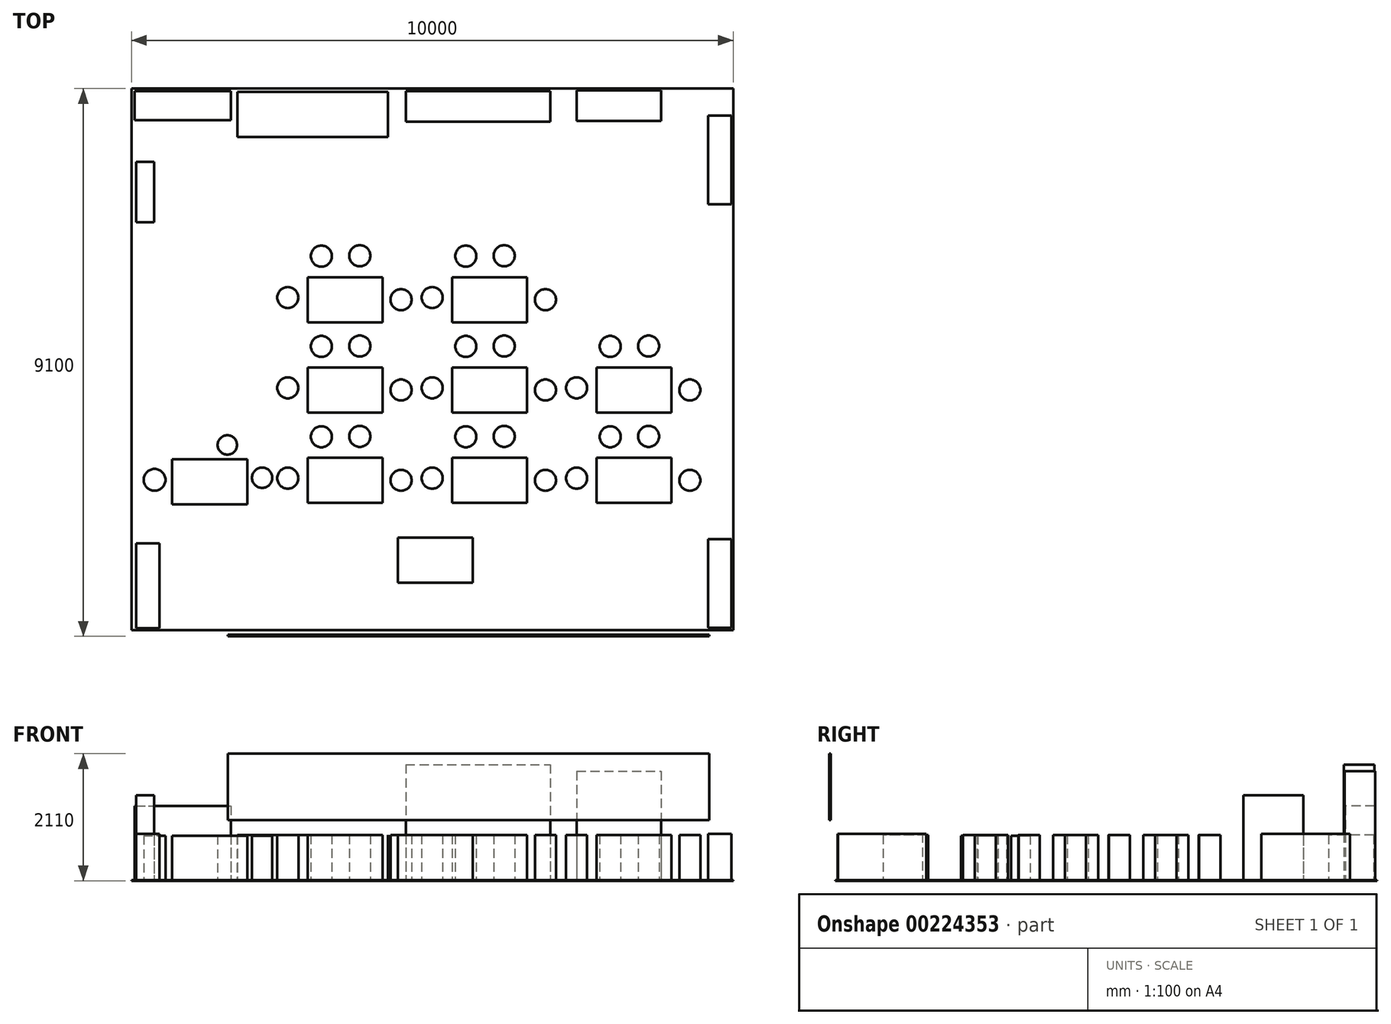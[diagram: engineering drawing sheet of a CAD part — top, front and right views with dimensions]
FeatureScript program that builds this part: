
annotation { "Feature Type Name" : "Feature", "Feature Type Description" : "" }
export const myFeature = defineFeature(function(context is Context, id is Id, definition is map)
    precondition{}
    {
        {
            var Q0;
            Q0=qCreatedBy(makeId("Top.planeOp"),FACE);
            var sketch = newSketch(context, id + "F0", { "sketchPlane" : qUnion([Q0])});
            skLineSegment(sketch, "E0.bottom", {"start": v(-5000, 4500) * mm, "end": v(5000, 4500) * mm});
            skLineSegment(sketch, "E0.top", {"start": v(-5000, -4500) * mm, "end": v(5000, -4500) * mm});
            skLineSegment(sketch, "E0.left", {"start": v(-5000, 4500) * mm, "end": v(-5000, -4500) * mm});
            skLineSegment(sketch, "E0.right", {"start": v(5000, 4500) * mm, "end": v(5000, -4500) * mm});
            skSolve(sketch);
        }
        {
            var Q0;
            Q0=makeQuery(id+"F0.imprint","IMPRINT",FACE,{"disambiguationData":[TD([[makeQuery(id+"F0.imprint","IMPRINT",EDGE,{"derivedFrom":sQuery(id+"F0.wireOp",EDGE,"E0.bottom")}),-1.0]])]});
            extrude(context, id + "F1", {"entities" : qUnion([Q0]), "oppositeDirection" : true, "depth" : 10 * mm});
        }
        {
            var Q0;
            Q0=qCreatedBy(makeId("Top.planeOp"),FACE);
            var sketch = newSketch(context, id + "F2", { "sketchPlane" : qUnion([Q0])});
            skLineSegment(sketch, "E1.bottom", {"start": v(-575.24, -2960.77) * mm, "end": v(674.76, -2960.77) * mm});
            skLineSegment(sketch, "E1.top", {"start": v(-575.24, -3710.77) * mm, "end": v(674.76, -3710.77) * mm});
            skLineSegment(sketch, "E1.left", {"start": v(-575.24, -2960.77) * mm, "end": v(-575.24, -3710.77) * mm});
            skLineSegment(sketch, "E1.right", {"start": v(674.76, -2960.77) * mm, "end": v(674.76, -3710.77) * mm});
            skLineSegment(sketch, "E2.bottom", {"start": v(2726.92, -1633.07) * mm, "end": v(3976.92, -1633.07) * mm});
            skLineSegment(sketch, "E2.top", {"start": v(2726.92, -2383.07) * mm, "end": v(3976.92, -2383.07) * mm});
            skLineSegment(sketch, "E2.left", {"start": v(2726.92, -1633.07) * mm, "end": v(2726.92, -2383.07) * mm});
            skLineSegment(sketch, "E2.right", {"start": v(3976.92, -1633.07) * mm, "end": v(3976.92, -2383.07) * mm});
            skCircle(sketch, "E3", {"center": v(3594.57, -1278.37) * mm, "radius": 175 * mm});
            skCircle(sketch, "E4", {"center": v(2398.6, -1972.2) * mm, "radius": 175 * mm});
            skCircle(sketch, "E5", {"center": v(2957.34, -1284.58) * mm, "radius": 175 * mm});
            skCircle(sketch, "E6", {"center": v(4280.4, -2008.07) * mm, "radius": 175 * mm});
            skCircle(sketch, "E7.0.1.0", {"center": v(3594.57, 221.63) * mm, "radius": 175 * mm});
            skCircle(sketch, "E7.0.1.1", {"center": v(4280.4, -508.07) * mm, "radius": 175 * mm});
            skLineSegment(sketch, "E7.0.1.2", {"start": v(3976.92, -133.07) * mm, "end": v(3976.92, -883.07) * mm});
            skCircle(sketch, "E7.0.1.3", {"center": v(2957.34, 215.42) * mm, "radius": 175 * mm});
            skLineSegment(sketch, "E7.0.1.4", {"start": v(2726.92, -133.07) * mm, "end": v(2726.92, -883.07) * mm});
            skCircle(sketch, "E7.0.1.5", {"center": v(2398.6, -472.2) * mm, "radius": 175 * mm});
            skLineSegment(sketch, "E7.0.1.6", {"start": v(2726.92, -883.07) * mm, "end": v(3976.92, -883.07) * mm});
            skLineSegment(sketch, "E7.0.1.7", {"start": v(2726.92, -133.07) * mm, "end": v(3976.92, -133.07) * mm});
            skCircle(sketch, "E7.1.0.0", {"center": v(1194.57, -1278.37) * mm, "radius": 175 * mm});
            skCircle(sketch, "E7.1.0.1", {"center": v(1880.4, -2008.07) * mm, "radius": 175 * mm});
            skLineSegment(sketch, "E7.1.0.2", {"start": v(1576.92, -1633.07) * mm, "end": v(1576.92, -2383.07) * mm});
            skCircle(sketch, "E7.1.0.3", {"center": v(557.34, -1284.58) * mm, "radius": 175 * mm});
            skLineSegment(sketch, "E7.1.0.4", {"start": v(326.92, -1633.07) * mm, "end": v(326.92, -2383.07) * mm});
            skCircle(sketch, "E7.1.0.5", {"center": v(-1.4, -1972.2) * mm, "radius": 175 * mm});
            skLineSegment(sketch, "E7.1.0.6", {"start": v(326.92, -2383.07) * mm, "end": v(1576.92, -2383.07) * mm});
            skLineSegment(sketch, "E7.1.0.7", {"start": v(326.92, -1633.07) * mm, "end": v(1576.92, -1633.07) * mm});
            skCircle(sketch, "E7.1.1.0", {"center": v(1194.57, 221.63) * mm, "radius": 175 * mm});
            skCircle(sketch, "E7.1.1.1", {"center": v(1880.4, -508.07) * mm, "radius": 175 * mm});
            skLineSegment(sketch, "E7.1.1.2", {"start": v(1576.92, -133.07) * mm, "end": v(1576.92, -883.07) * mm});
            skCircle(sketch, "E7.1.1.3", {"center": v(557.34, 215.42) * mm, "radius": 175 * mm});
            skLineSegment(sketch, "E7.1.1.4", {"start": v(326.92, -133.07) * mm, "end": v(326.92, -883.07) * mm});
            skCircle(sketch, "E7.1.1.5", {"center": v(-1.4, -472.2) * mm, "radius": 175 * mm});
            skLineSegment(sketch, "E7.1.1.6", {"start": v(326.92, -883.07) * mm, "end": v(1576.92, -883.07) * mm});
            skLineSegment(sketch, "E7.1.1.7", {"start": v(326.92, -133.07) * mm, "end": v(1576.92, -133.07) * mm});
            skCircle(sketch, "E7.1.2.0", {"center": v(1194.57, 1721.63) * mm, "radius": 175 * mm});
            skCircle(sketch, "E7.1.2.1", {"center": v(1880.4, 991.93) * mm, "radius": 175 * mm});
            skLineSegment(sketch, "E7.1.2.2", {"start": v(1576.92, 1366.93) * mm, "end": v(1576.92, 616.93) * mm});
            skCircle(sketch, "E7.1.2.3", {"center": v(557.34, 1715.42) * mm, "radius": 175 * mm});
            skLineSegment(sketch, "E7.1.2.4", {"start": v(326.92, 1366.93) * mm, "end": v(326.92, 616.93) * mm});
            skCircle(sketch, "E7.1.2.5", {"center": v(-1.4, 1027.8) * mm, "radius": 175 * mm});
            skLineSegment(sketch, "E7.1.2.6", {"start": v(326.92, 616.93) * mm, "end": v(1576.92, 616.93) * mm});
            skLineSegment(sketch, "E7.1.2.7", {"start": v(326.92, 1366.93) * mm, "end": v(1576.92, 1366.93) * mm});
            skCircle(sketch, "E7.2.0.0", {"center": v(-1205.43, -1278.37) * mm, "radius": 175 * mm});
            skCircle(sketch, "E7.2.0.1", {"center": v(-519.6, -2008.07) * mm, "radius": 175 * mm});
            skLineSegment(sketch, "E7.2.0.2", {"start": v(-823.08, -1633.07) * mm, "end": v(-823.08, -2383.07) * mm});
            skCircle(sketch, "E7.2.0.3", {"center": v(-1842.66, -1284.58) * mm, "radius": 175 * mm});
            skLineSegment(sketch, "E7.2.0.4", {"start": v(-2073.08, -1633.07) * mm, "end": v(-2073.08, -2383.07) * mm});
            skCircle(sketch, "E7.2.0.5", {"center": v(-2401.4, -1972.2) * mm, "radius": 175 * mm});
            skLineSegment(sketch, "E7.2.0.6", {"start": v(-2073.08, -2383.07) * mm, "end": v(-823.08, -2383.07) * mm});
            skLineSegment(sketch, "E7.2.0.7", {"start": v(-2073.08, -1633.07) * mm, "end": v(-823.08, -1633.07) * mm});
            skCircle(sketch, "E7.2.1.0", {"center": v(-1205.43, 221.63) * mm, "radius": 175 * mm});
            skCircle(sketch, "E7.2.1.1", {"center": v(-519.6, -508.07) * mm, "radius": 175 * mm});
            skLineSegment(sketch, "E7.2.1.2", {"start": v(-823.08, -133.07) * mm, "end": v(-823.08, -883.07) * mm});
            skCircle(sketch, "E7.2.1.3", {"center": v(-1842.66, 215.42) * mm, "radius": 175 * mm});
            skLineSegment(sketch, "E7.2.1.4", {"start": v(-2073.08, -133.07) * mm, "end": v(-2073.08, -883.07) * mm});
            skCircle(sketch, "E7.2.1.5", {"center": v(-2401.4, -472.2) * mm, "radius": 175 * mm});
            skLineSegment(sketch, "E7.2.1.6", {"start": v(-2073.08, -883.07) * mm, "end": v(-823.08, -883.07) * mm});
            skLineSegment(sketch, "E7.2.1.7", {"start": v(-2073.08, -133.07) * mm, "end": v(-823.08, -133.07) * mm});
            skCircle(sketch, "E7.2.2.0", {"center": v(-1205.43, 1721.63) * mm, "radius": 175 * mm});
            skCircle(sketch, "E7.2.2.1", {"center": v(-519.6, 991.93) * mm, "radius": 175 * mm});
            skLineSegment(sketch, "E7.2.2.2", {"start": v(-823.08, 1366.93) * mm, "end": v(-823.08, 616.93) * mm});
            skCircle(sketch, "E7.2.2.3", {"center": v(-1842.66, 1715.42) * mm, "radius": 175 * mm});
            skLineSegment(sketch, "E7.2.2.4", {"start": v(-2073.08, 1366.93) * mm, "end": v(-2073.08, 616.93) * mm});
            skCircle(sketch, "E7.2.2.5", {"center": v(-2401.4, 1027.8) * mm, "radius": 175 * mm});
            skLineSegment(sketch, "E7.2.2.6", {"start": v(-2073.08, 616.93) * mm, "end": v(-823.08, 616.93) * mm});
            skLineSegment(sketch, "E7.2.2.7", {"start": v(-2073.08, 1366.93) * mm, "end": v(-823.08, 1366.93) * mm});
            skLineSegment(sketch, "E7.direction1", {"start": v(2726.92, -2383.07) * mm, "end": v(326.92, -2383.07) * mm, "construction": true});
            skLineSegment(sketch, "E7.direction2", {"start": v(2726.92, -2383.07) * mm, "end": v(2726.92, -883.07) * mm, "construction": true});
            skPoint(sketch, "E8", {"position": v(3976.92, -508.07) * mm});
            skSolve(sketch);
        }
        {
            var Q0;
            Q0=qSketchRegion(id+"F2",true);
            extrude(context, id + "F3", {"entities" : qUnion([Q0]), "operationType" : NewBodyOperationType.ADD, "depth" : 750 * mm});
        }
        {
            var Q0;
            Q0=qCreatedBy(makeId("Front.planeOp"),FACE);
            cPlane(context, id + "F4", {"entities" : qUnion([Q0]), "cplaneType" : CPlaneType.OFFSET, "offset" : 4500 * mm, "width" : 150 * mm, "height" : 150 * mm});
        }
        {
            var Q0;
            Q0=qCreatedBy(id+"F4.planeOp",FACE);
            var sketch = newSketch(context, id + "F5", { "sketchPlane" : qUnion([Q0])});
            skLineSegment(sketch, "E9.bottom", {"start": v(-3400, 2100) * mm, "end": v(4600, 2100) * mm});
            skLineSegment(sketch, "E9.top", {"start": v(-3400, 1000) * mm, "end": v(4600, 1000) * mm});
            skLineSegment(sketch, "E9.left", {"start": v(-3400, 2100) * mm, "end": v(-3400, 1000) * mm});
            skLineSegment(sketch, "E9.right", {"start": v(4600, 2100) * mm, "end": v(4600, 1000) * mm});
            skSolve(sketch);
        }
        {
            var Q0;
            Q0=qSketchRegion(id+"F5",true);
            extrude(context, id + "F6", {"entities" : qUnion([Q0]), "oppositeDirection" : true, "depth" : 25 * mm});
        }
        {
            var Q0;
            Q0=qCreatedBy(makeId("Top.planeOp"),FACE);
            var sketch = newSketch(context, id + "F7", { "sketchPlane" : qUnion([Q0])});
            skLineSegment(sketch, "E10.bottom", {"start": v(-4950, 4456.62) * mm, "end": v(-4150, 4456.62) * mm});
            skLineSegment(sketch, "E10.top", {"start": v(-4950, 3976.62) * mm, "end": v(-4150, 3976.62) * mm});
            skLineSegment(sketch, "E10.left", {"start": v(-4950, 4456.62) * mm, "end": v(-4950, 3976.62) * mm});
            skLineSegment(sketch, "E10.right", {"start": v(-4150, 4456.62) * mm, "end": v(-4150, 3976.62) * mm});
            skLineSegment(sketch, "E11.bottom", {"start": v(-4150, 4456.62) * mm, "end": v(-3350, 4456.62) * mm});
            skLineSegment(sketch, "E11.top", {"start": v(-4150, 3976.62) * mm, "end": v(-3350, 3976.62) * mm});
            skLineSegment(sketch, "E11.right", {"start": v(-3350, 4456.62) * mm, "end": v(-3350, 3976.62) * mm});
            skSolve(sketch);
        }
        {
            var Q0;
            Q0=qSketchRegion(id+"F7",true);
            extrude(context, id + "F8", {"entities" : qUnion([Q0]), "operationType" : NewBodyOperationType.ADD, "depth" : 1230 * mm});
        }
        {
            var Q0;
            Q0=qCreatedBy(makeId("Top.planeOp"),FACE);
            var sketch = newSketch(context, id + "F9", { "sketchPlane" : qUnion([Q0])});
            skLineSegment(sketch, "E12.bottom", {"start": v(2400, 3961.01) * mm, "end": v(3800, 3961.01) * mm});
            skLineSegment(sketch, "E12.top", {"start": v(2400, 4471.01) * mm, "end": v(3800, 4471.01) * mm});
            skLineSegment(sketch, "E12.left", {"start": v(2400, 3961.01) * mm, "end": v(2400, 4471.01) * mm});
            skLineSegment(sketch, "E12.right", {"start": v(3800, 3961.01) * mm, "end": v(3800, 4471.01) * mm});
            skSolve(sketch);
        }
        {
            var Q0;
            Q0=qSketchRegion(id+"F9",true);
            extrude(context, id + "F10", {"entities" : qUnion([Q0]), "operationType" : NewBodyOperationType.ADD, "depth" : 1810 * mm});
        }
        {
            var Q0;
            Q0=makeQuery(id+"F1.opExtrude","SWEPT_BODY",BODY,{"disambiguationData":[OSD([sQuery(id+"F0.wireOp",EDGE,"E0.bottom"),sQuery(id+"F0.wireOp",EDGE,"E0.top"),sQuery(id+"F0.wireOp",EDGE,"E0.left"),sQuery(id+"F0.wireOp",EDGE,"E0.right")])]});
            transform(context, id + "F11", {"entities" : qUnion([Q0]), "transformType" : TransformType.TRANSLATION_3D, "dx" : 0 * mm, "dy" : 100 * mm, "dz" : 0 * mm, "makeCopy" : false});
        }
        {
            var Q0;
            Q0=qCreatedBy(makeId("Top.planeOp"),FACE);
            var sketch = newSketch(context, id + "F12", { "sketchPlane" : qUnion([Q0])});
            skLineSegment(sketch, "E13.bottom", {"start": v(-3240.14, 4545.7) * mm, "end": v(-740.14, 4545.7) * mm});
            skLineSegment(sketch, "E13.top", {"start": v(-3240.14, 3795.7) * mm, "end": v(-740.14, 3795.7) * mm});
            skLineSegment(sketch, "E13.left", {"start": v(-3240.14, 4545.7) * mm, "end": v(-3240.14, 3795.7) * mm});
            skLineSegment(sketch, "E13.right", {"start": v(-740.14, 4545.7) * mm, "end": v(-740.14, 3795.7) * mm});
            skSolve(sketch);
        }
        {
            var Q0;
            Q0 = qSketchRegion(id + "F12", true);
            extrude(context, id + "F13", {"entities" : qUnion([Q0]), "operationType" : NewBodyOperationType.ADD, "depth" : 750 * mm});
        }
        {
            var Q0;
            Q0=qCreatedBy(makeId("Top.planeOp"),FACE);
            var sketch = newSketch(context, id + "F14", { "sketchPlane" : qUnion([Q0])});
            skLineSegment(sketch, "E14.bottom", {"start": v(-4326.15, -1559.53) * mm, "end": v(-3076.15, -1559.53) * mm});
            skLineSegment(sketch, "E14.top", {"start": v(-4326.15, -2309.53) * mm, "end": v(-3076.15, -2309.53) * mm});
            skLineSegment(sketch, "E14.left", {"start": v(-4326.15, -1559.53) * mm, "end": v(-4326.15, -2309.53) * mm});
            skLineSegment(sketch, "E14.right", {"start": v(-3076.15, -1559.53) * mm, "end": v(-3076.15, -2309.53) * mm});
            skSolve(sketch);
        }
        {
            var Q0;
            Q0 = qSketchRegion(id + "F14", true);
            extrude(context, id + "F15", {"entities" : qUnion([Q0]), "operationType" : NewBodyOperationType.ADD, "depth" : 740 * mm});
        }
        {
            var Q0;
            Q0=qCreatedBy(makeId("Top.planeOp"),FACE);
            var sketch = newSketch(context, id + "F16", { "sketchPlane" : qUnion([Q0])});
            skCircle(sketch, "E15", {"center": v(-3406.42, -1321.08) * mm, "radius": 160.68 * mm});
            skCircle(sketch, "E16", {"center": v(-4615.7, -1900.17) * mm, "radius": 181.05 * mm});
            skCircle(sketch, "E17", {"center": v(-2827.33, -1866.1) * mm, "radius": 168.6 * mm});
            skSolve(sketch);
        }
        {
            var Q0;
            Q0=makeQuery(id+"F16.imprint","IMPRINT",FACE,{"disambiguationData":[TD([[makeQuery(id+"F16.imprint","IMPRINT",EDGE,{"derivedFrom":sQuery(id+"F16.wireOp",EDGE,"E17")}),1.0]])]});
            var Q1;
            Q1=makeQuery(id+"F16.imprint","IMPRINT",FACE,{"disambiguationData":[TD([[makeQuery(id+"F16.imprint","IMPRINT",EDGE,{"derivedFrom":sQuery(id+"F16.wireOp",EDGE,"E15")}),1.0]])]});
            var Q2;
            Q2=makeQuery(id+"F16.imprint","IMPRINT",FACE,{"disambiguationData":[TD([[makeQuery(id+"F16.imprint","IMPRINT",EDGE,{"derivedFrom":sQuery(id+"F16.wireOp",EDGE,"E16")}),1.0]])]});
            extrude(context, id + "F17", {"entities" : qUnion([Q0, Q1, Q2]), "operationType" : NewBodyOperationType.ADD, "depth" : 740 * mm});
        }
        {
            var Q0;
            Q0=qCreatedBy(makeId("Top.planeOp"),FACE);
            var sketch = newSketch(context, id + "F18", { "sketchPlane" : qUnion([Q0])});
            skLineSegment(sketch, "E18.bottom", {"start": v(-440.14, 4558.86) * mm, "end": v(1959.86, 4558.86) * mm});
            skLineSegment(sketch, "E18.top", {"start": v(-440.14, 4048.86) * mm, "end": v(1959.86, 4048.86) * mm});
            skLineSegment(sketch, "E18.left", {"start": v(-440.14, 4558.86) * mm, "end": v(-440.14, 4048.86) * mm});
            skLineSegment(sketch, "E18.right", {"start": v(1959.86, 4558.86) * mm, "end": v(1959.86, 4048.86) * mm});
            skSolve(sketch);
        }
        {
            var Q0;
            Q0 = qSketchRegion(id + "F18", true);
            extrude(context, id + "F19", {"entities" : qUnion([Q0]), "operationType" : NewBodyOperationType.ADD, "depth" : 1920 * mm});
        }
        {
            var Q0;
            Q0=qCreatedBy(makeId("Top.planeOp"),FACE);
            var sketch = newSketch(context, id + "F20", { "sketchPlane" : qUnion([Q0])});
            skLineSegment(sketch, "E19.bottom", {"start": v(4583.59, 4149.91) * mm, "end": v(4973.59, 4149.91) * mm});
            skLineSegment(sketch, "E19.top", {"start": v(4583.59, 2679.91) * mm, "end": v(4973.59, 2679.91) * mm});
            skLineSegment(sketch, "E19.left", {"start": v(4583.59, 4149.91) * mm, "end": v(4583.59, 2679.91) * mm});
            skLineSegment(sketch, "E19.right", {"start": v(4973.59, 4149.91) * mm, "end": v(4973.59, 2679.91) * mm});
            skSolve(sketch);
        }
        {
            var Q0;
            Q0 = qSketchRegion(id + "F20", true);
            extrude(context, id + "F21", {"entities" : qUnion([Q0]), "operationType" : NewBodyOperationType.ADD, "depth" : 770 * mm});
        }
        {
            var Q0;
            Q0=qCreatedBy(makeId("Top.planeOp"),FACE);
            var sketch = newSketch(context, id + "F22", { "sketchPlane" : qUnion([Q0])});
            skLineSegment(sketch, "E20.bottom", {"start": v(4581.63, -2888.03) * mm, "end": v(4971.63, -2888.03) * mm});
            skLineSegment(sketch, "E20.top", {"start": v(4581.63, -4358.03) * mm, "end": v(4971.63, -4358.03) * mm});
            skLineSegment(sketch, "E20.left", {"start": v(4581.63, -2888.03) * mm, "end": v(4581.63, -4358.03) * mm});
            skLineSegment(sketch, "E20.right", {"start": v(4971.63, -2888.03) * mm, "end": v(4971.63, -4358.03) * mm});
            skSolve(sketch);
        }
        {
            var Q0;
            Q0 = qSketchRegion(id + "F22", true);
            extrude(context, id + "F23", {"entities" : qUnion([Q0]), "operationType" : NewBodyOperationType.ADD, "depth" : 770 * mm});
        }
        {
            var Q0;
            Q0=qCreatedBy(makeId("Right.planeOp"),FACE);
            var sketch = newSketch(context, id + "F24", { "sketchPlane" : qUnion([Q0])});
            skLineSegment(sketch, "E21.bottom", {"start": v(-1200, 2396.74) * mm, "end": v(0, 2396.74) * mm});
            skLineSegment(sketch, "E21.top", {"start": v(-1200, 1396.74) * mm, "end": v(0, 1396.74) * mm});
            skLineSegment(sketch, "E21.left", {"start": v(-1200, 2396.74) * mm, "end": v(-1200, 1396.74) * mm});
            skLineSegment(sketch, "E21.right", {"start": v(0, 2396.74) * mm, "end": v(0, 1396.74) * mm});
            skSolve(sketch);
        }
        {
            var Q0;
            Q0=qCreatedBy(makeId("Top.planeOp"),FACE);
            var sketch = newSketch(context, id + "F25", { "sketchPlane" : qUnion([Q0])});
            skLineSegment(sketch, "E22.bottom", {"start": v(-4922.27, 3379.77) * mm, "end": v(-4622.27, 3379.77) * mm});
            skLineSegment(sketch, "E22.top", {"start": v(-4922.27, 2379.77) * mm, "end": v(-4622.27, 2379.77) * mm});
            skLineSegment(sketch, "E22.left", {"start": v(-4922.27, 3379.77) * mm, "end": v(-4922.27, 2379.77) * mm});
            skLineSegment(sketch, "E22.right", {"start": v(-4622.27, 3379.77) * mm, "end": v(-4622.27, 2379.77) * mm});
            skSolve(sketch);
        }
        {
            var Q0;
            Q0 = qSketchRegion(id + "F25", true);
            extrude(context, id + "F26", {"entities" : qUnion([Q0]), "operationType" : NewBodyOperationType.ADD, "depth" : 1410 * mm});
        }
        {
            var Q0;
            Q0=qCreatedBy(makeId("Top.planeOp"),FACE);
            var sketch = newSketch(context, id + "F27", { "sketchPlane" : qUnion([Q0])});
            skLineSegment(sketch, "E23.bottom", {"start": v(-4922.27, -2956.16) * mm, "end": v(-4532.27, -2956.16) * mm});
            skLineSegment(sketch, "E23.top", {"start": v(-4922.27, -4366.16) * mm, "end": v(-4532.27, -4366.16) * mm});
            skLineSegment(sketch, "E23.left", {"start": v(-4922.27, -2956.16) * mm, "end": v(-4922.27, -4366.16) * mm});
            skLineSegment(sketch, "E23.right", {"start": v(-4532.27, -2956.16) * mm, "end": v(-4532.27, -4366.16) * mm});
            skSolve(sketch);
        }
        {
            var Q0;
            Q0 = qSketchRegion(id + "F27", true);
            extrude(context, id + "F28", {"entities" : qUnion([Q0]), "operationType" : NewBodyOperationType.ADD, "depth" : 770 * mm});
        }
    });
